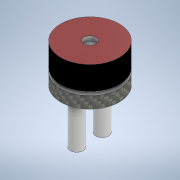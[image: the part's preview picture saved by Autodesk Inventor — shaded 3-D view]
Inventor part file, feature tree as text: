
AUTODESK INVENTOR PART (.ipt)
format: ipt  version: 2021 (Build 250183000, 183)  size: 133,632 bytes
history: native  units: mm
features: sketch x5, extrude x4, hole x1
ambient origin geometry x8: Origin, YZ Plane, XZ Plane, XY Plane, X Axis, Y Axis, Z Axis, Center Point
bodies: Solid1 (feature_tree)
feature tree (10):
  extrude  "Extrusion1"  Depth=10.0mm TaperAngle=0.0deg
  extrude  "Extrusion2"  Depth=20.0mm TaperAngle=0.0deg
  extrude  "Extrusion3"  [1 undecoded]
  extrude  "Extrusion4"  [1 undecoded]
  hole  "Hole1"  [1 undecoded]
  sketch  "Sketch1"  dims[d0=50.0mm d1=10.0mm d2=0.0mm]
  sketch  "Sketch2"  dims[d3=3.0mm d4=0.0mm d5=20.0mm d6=0.0mm]
  sketch  "Sketch3"  dims[d7=40.0mm d8=0.0mm]
  sketch  "Sketch4"  dims[d9=10.0mm d10=6.0mm d11=4.0mm d12=2.0mm d13=90.0deg d14=4.0mm d15=0.0mm]
  sketch  "Sketch5"
note: 3 required parameter values undecoded (feature->parameter linkage not recoverable at this tier; creation-order binding heuristic only, values carry confidence <= 0.55)
